# Revit family: Mobile-Work-Tools-Teknion-HDWR_Recycle_Kiosk-R2020
name_source: partatom
category: Furniture
units: mm (PartAtom-declared; Revit-internal decimal feet)

## family parameters
Always vertical = Yes
Cut with Voids When Loaded = No
OmniClass Number = 23.40.20.00
OmniClass Title = General Furniture and Specialties
Room Calculation Point = No
Shared = Yes
Work Plane-Based = No

## types (2) — shared parameters
Assembly Code = E2020200
Manufacturer = Teknion
Manufacturer Fax = 416.661.4586
Part Number = HDWR
Product Documentation Link = https://assets.teknion.com
Product Line = Kiosk
Product Page URL = https://www.teknion.com
Series = Kiosk
Sustainability Data = https://www.teknion.com
URL = www.teknion.com
Unit Weight URL = http://www.teknion.com
Warranty = http://www.teknion.com
zero-valued in all types: Default Elevation

## per-type parameters (varying)
| type | Description | Ledge | Model |
| No Ledge | Recycle Kiosk, 72" Height, 60" Width, Bins Configuration, No Ledge | No | HDWR7260BN |
| With Ledge | Recycle Kiosk, 72" Height, 60" Width, Bins Configuration, With Ledge | Yes | HDWR7260BY |

## geometry (parser evidence)
native form markers: Sweep x4
no freeform markers — native parametric forms only
